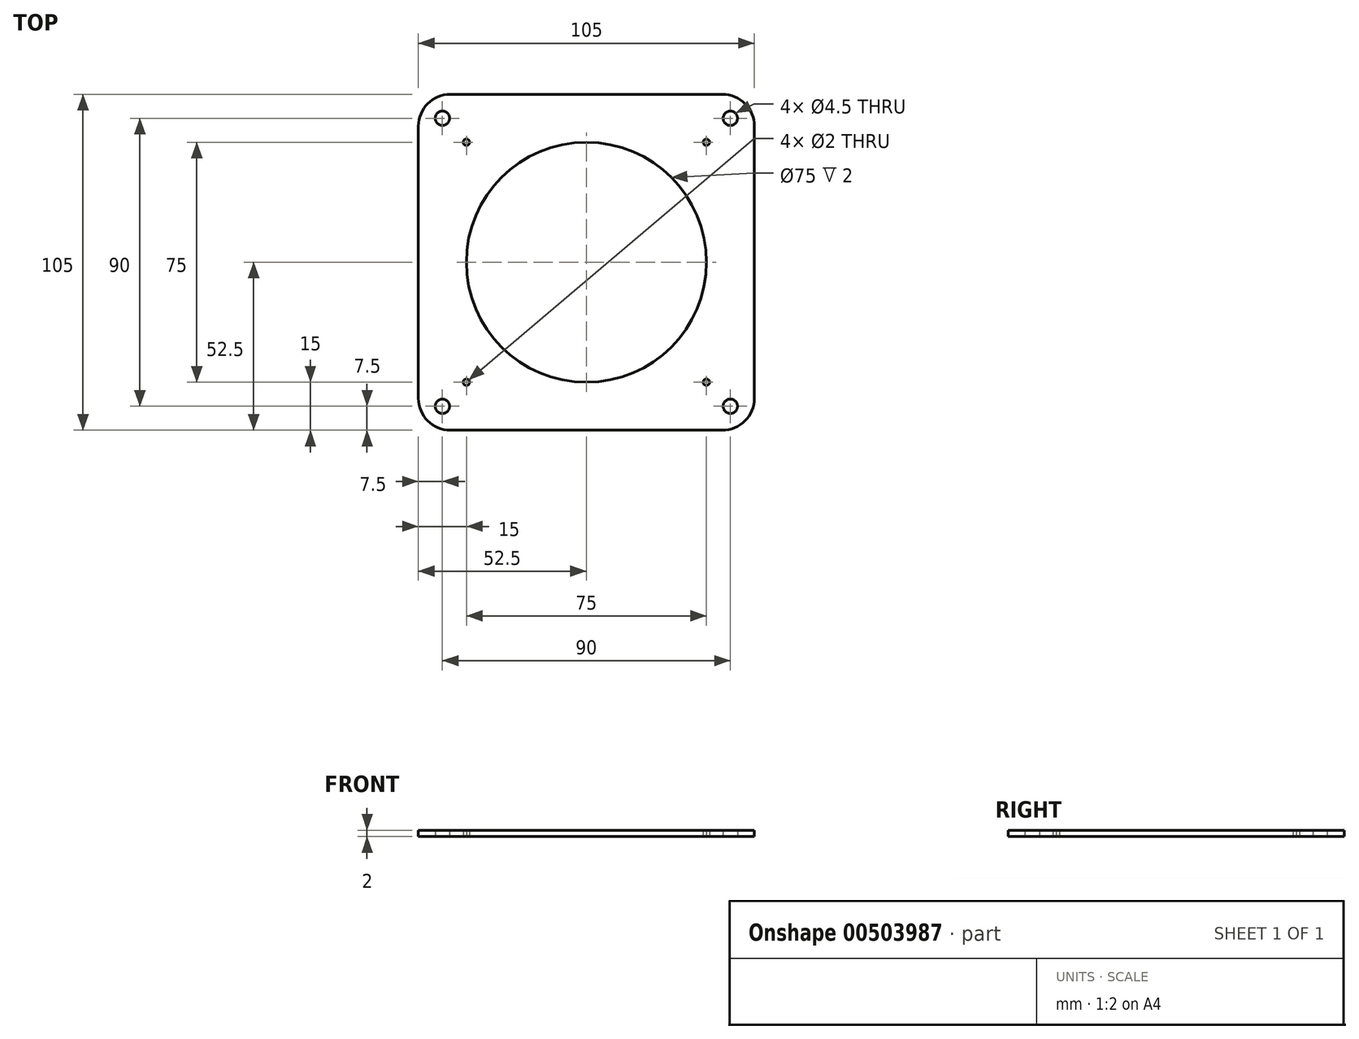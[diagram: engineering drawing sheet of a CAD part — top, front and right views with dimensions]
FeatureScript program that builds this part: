
annotation { "Feature Type Name" : "Feature", "Feature Type Description" : "" }
export const myFeature = defineFeature(function(context is Context, id is Id, definition is map)
    precondition{}
    {
        {
            var Q0;
            Q0=qCreatedBy(makeId("Top.planeOp"),FACE);
            var sketch = newSketch(context, id + "F0", { "sketchPlane" : qUnion([Q0])});
            skLineSegment(sketch, "E0.bottom", {"start": v(-42.5, 52.5) * mm, "end": v(42.5, 52.5) * mm});
            skLineSegment(sketch, "E0.top", {"start": v(-42.5, -52.5) * mm, "end": v(42.5, -52.5) * mm});
            skLineSegment(sketch, "E0.left", {"start": v(-52.5, 42.5) * mm, "end": v(-52.5, -42.5) * mm});
            skLineSegment(sketch, "E0.right", {"start": v(52.5, 42.5) * mm, "end": v(52.5, -42.5) * mm});
            skCircle(sketch, "E1", {"center": v(-45, 45) * mm, "radius": 2.25 * mm});
            skCircle(sketch, "E2", {"center": v(45, 45) * mm, "radius": 2.25 * mm});
            skCircle(sketch, "E3", {"center": v(-45, -45) * mm, "radius": 2.25 * mm});
            skCircle(sketch, "E4", {"center": v(45, -45) * mm, "radius": 2.25 * mm});
            skLineSegment(sketch, "E5", {"start": v(0, 52.5) * mm, "end": v(0, 0) * mm, "construction": true});
            skLineSegment(sketch, "E6", {"start": v(-52.5, 0) * mm, "end": v(0, 0) * mm, "construction": true});
            skLineSegment(sketch, "E7.bottom", {"start": v(-37.5, 37.5) * mm, "end": v(37.5, 37.5) * mm, "construction": true});
            skLineSegment(sketch, "E7.top", {"start": v(-37.5, -37.5) * mm, "end": v(37.5, -37.5) * mm, "construction": true});
            skLineSegment(sketch, "E7.left", {"start": v(-37.5, 37.5) * mm, "end": v(-37.5, -37.5) * mm, "construction": true});
            skLineSegment(sketch, "E7.right", {"start": v(37.5, 37.5) * mm, "end": v(37.5, -37.5) * mm, "construction": true});
            skLineSegment(sketch, "E8", {"start": v(-52.5, 52.5) * mm, "end": v(52.5, -52.5) * mm, "construction": true});
            skLineSegment(sketch, "E9", {"start": v(37.5, 37.5) * mm, "end": v(-37.5, -37.5) * mm, "construction": true});
            skCircle(sketch, "E10", {"center": v(-37.5, 37.5) * mm, "radius": 1 * mm});
            skCircle(sketch, "E11", {"center": v(37.5, 37.5) * mm, "radius": 1 * mm});
            skCircle(sketch, "E12", {"center": v(-37.5, -37.5) * mm, "radius": 1 * mm});
            skCircle(sketch, "E13", {"center": v(37.5, -37.5) * mm, "radius": 1 * mm});
            skCircle(sketch, "E14", {"center": v(0, 0) * mm, "radius": 37.5 * mm});
            skPoint(sketch, "E15.visualSharp", {"position": v(-52.5, 52.5) * mm});
            skArc(sketch, "E15.filletArc", {"start": v(-42.5, 52.5) * mm, "mid": v(-49.57, 49.57) * mm, "end": v(-52.5, 42.5) * mm});
            skPoint(sketch, "E16.visualSharp", {"position": v(52.5, 52.5) * mm});
            skArc(sketch, "E16.filletArc", {"start": v(52.5, 42.5) * mm, "mid": v(49.57, 49.57) * mm, "end": v(42.5, 52.5) * mm});
            skPoint(sketch, "E17.visualSharp", {"position": v(52.5, -52.5) * mm});
            skArc(sketch, "E17.filletArc", {"start": v(42.5, -52.5) * mm, "mid": v(49.57, -49.57) * mm, "end": v(52.5, -42.5) * mm});
            skPoint(sketch, "E18.visualSharp", {"position": v(-52.5, -52.5) * mm});
            skArc(sketch, "E18.filletArc", {"start": v(-52.5, -42.5) * mm, "mid": v(-49.57, -49.57) * mm, "end": v(-42.5, -52.5) * mm});
            skSolve(sketch);
        }
        {
            var Q0;
            Q0=makeQuery(id+"F0.imprint","IMPRINT",FACE,{"disambiguationData":[TD([[makeQuery(id+"F0.imprint","IMPRINT",EDGE,{"derivedFrom":sQuery(id+"F0.wireOp",EDGE,"E0.bottom")}),-1.0]])]});
            extrude(context, id + "F1", {"entities" : qUnion([Q0]), "depth" : 2 * mm, "offsetDistance" : 25 * mm});
        }
    });
